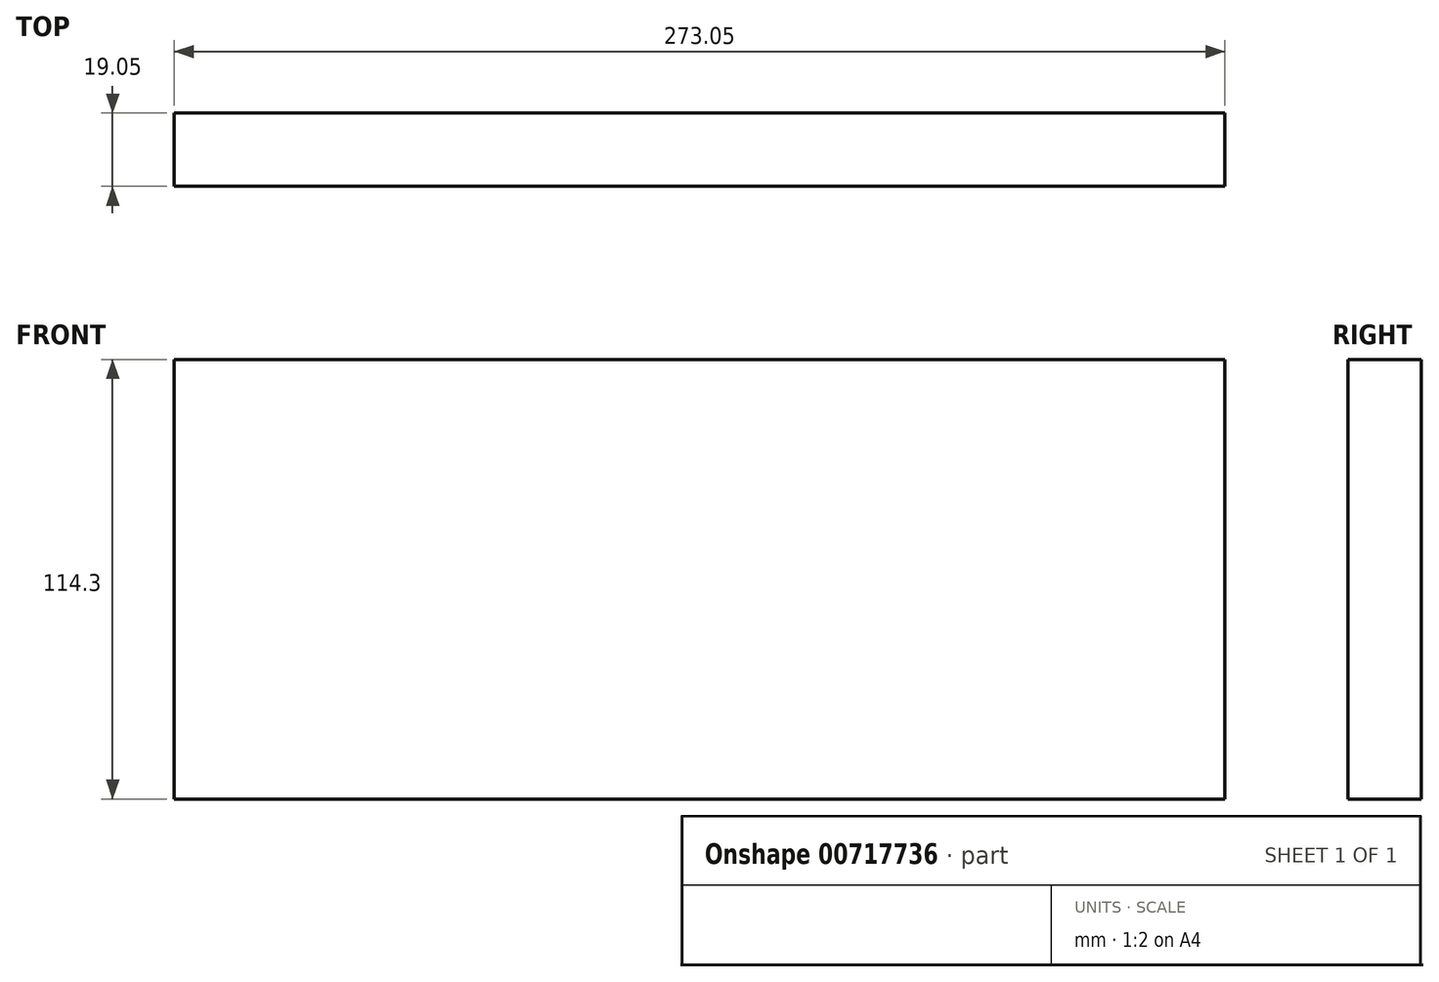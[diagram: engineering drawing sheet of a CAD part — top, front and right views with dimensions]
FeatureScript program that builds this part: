
annotation { "Feature Type Name" : "Feature", "Feature Type Description" : "" }
export const myFeature = defineFeature(function(context is Context, id is Id, definition is map)
    precondition{}
    {
        {
            var Q0;
            Q0=qCreatedBy(makeId("Front.planeOp"),FACE);
            var sketch = newSketch(context, id + "F0", { "sketchPlane" : qUnion([Q0])});
            skLineSegment(sketch, "E0.bottom", {"start": v(-129.65, 64.71) * mm, "end": v(143.4, 64.71) * mm});
            skLineSegment(sketch, "E0.top", {"start": v(-129.65, -49.59) * mm, "end": v(143.4, -49.59) * mm});
            skLineSegment(sketch, "E0.left", {"start": v(-129.65, 64.71) * mm, "end": v(-129.65, -49.59) * mm});
            skLineSegment(sketch, "E0.right", {"start": v(143.4, 64.71) * mm, "end": v(143.4, -49.59) * mm});
            skSolve(sketch);
        }
        {
            var Q0;
            Q0=qSketchRegion(id+"F0",true);
            extrude(context, id + "F1", {"entities" : qUnion([Q0]), "depth" : 19.05 * mm, "offsetDistance" : 25.4 * mm});
        }
    });
